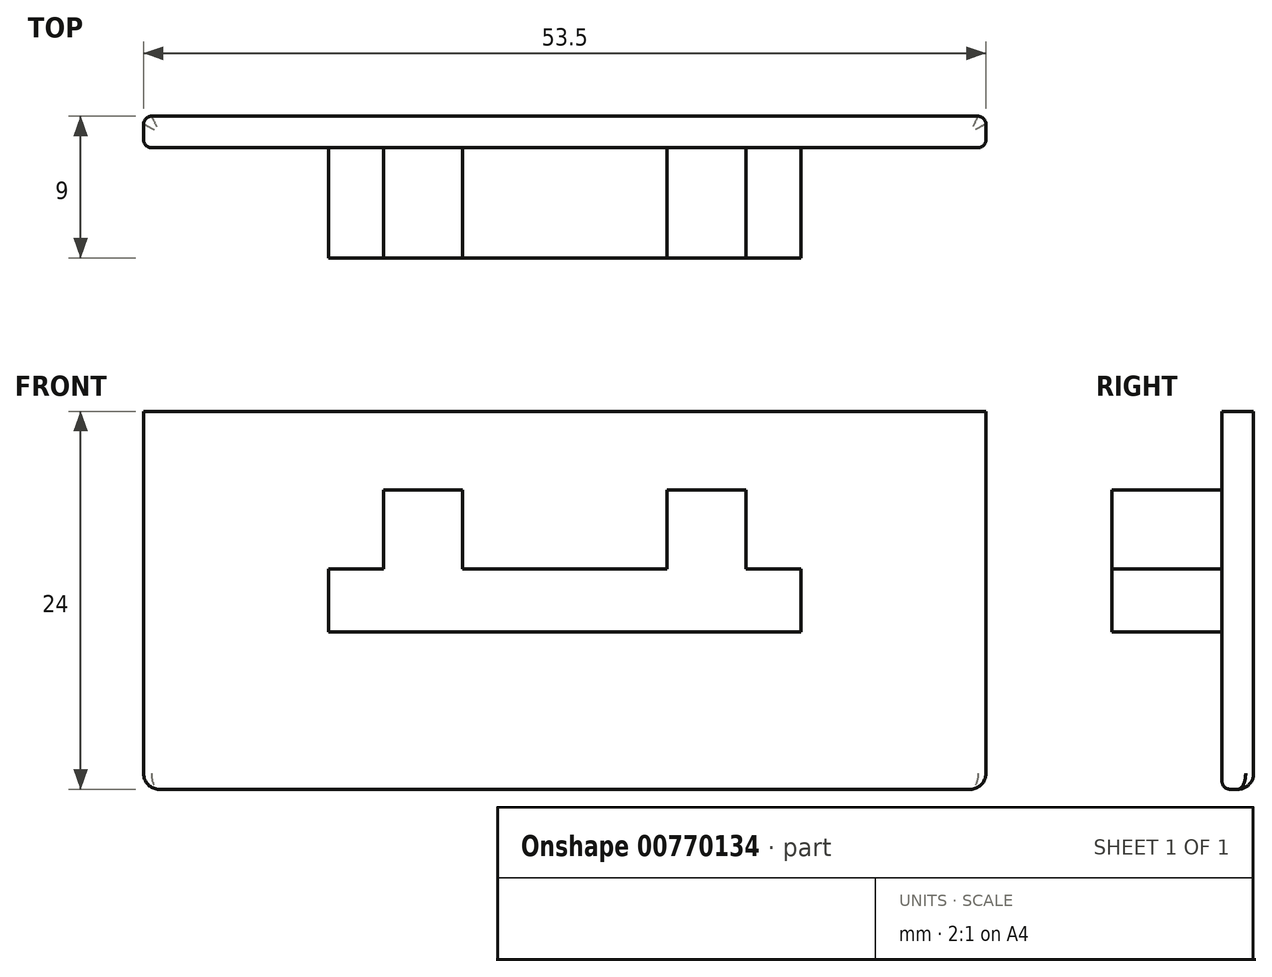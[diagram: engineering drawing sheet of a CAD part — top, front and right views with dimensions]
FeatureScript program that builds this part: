
annotation { "Feature Type Name" : "Feature", "Feature Type Description" : "" }
export const myFeature = defineFeature(function(context is Context, id is Id, definition is map)
    precondition{}
    {
        {
            var Q0;
            Q0=qCreatedBy(makeId("Front.planeOp"),FACE);
            var sketch = newSketch(context, id + "F0", { "sketchPlane" : qUnion([Q0])});
            skLineSegment(sketch, "E0.bottom", {"start": v(0, 0) * mm, "end": v(53.5, 0) * mm});
            skLineSegment(sketch, "E0.top", {"start": v(0, 24) * mm, "end": v(53.5, 24) * mm});
            skLineSegment(sketch, "E0.left", {"start": v(0, 0) * mm, "end": v(0, 24) * mm});
            skLineSegment(sketch, "E0.right", {"start": v(53.5, 0) * mm, "end": v(53.5, 24) * mm});
            skSolve(sketch);
        }
        {
            var Q0;
            Q0=qSketchRegion(id+"F0",true);
            extrude(context, id + "F1", {"entities" : qUnion([Q0]), "depth" : 2 * mm, "offsetDistance" : 25 * mm});
        }
        {
            var Q0;
            Q0=makeQuery(id+"F1.opExtrude","CAP_FACE",FACE,{"disambiguationData":[OSD([sQuery(id+"F0.wireOp",EDGE,"E0.bottom"),sQuery(id+"F0.wireOp",EDGE,"E0.top"),sQuery(id+"F0.wireOp",EDGE,"E0.left"),sQuery(id+"F0.wireOp",EDGE,"E0.right")])],"isStart":false});
            var sketch = newSketch(context, id + "F2", { "sketchPlane" : qUnion([Q0])});
            skLineSegment(sketch, "E1.bottom", {"start": v(11.75, 14) * mm, "end": v(15.25, 14) * mm});
            skLineSegment(sketch, "E1.top", {"start": v(11.75, 10) * mm, "end": v(41.75, 10) * mm});
            skLineSegment(sketch, "E1.left", {"start": v(11.75, 14) * mm, "end": v(11.75, 10) * mm});
            skLineSegment(sketch, "E1.right", {"start": v(41.75, 14) * mm, "end": v(41.75, 10) * mm});
            skLineSegment(sketch, "E2.top", {"start": v(38.25, 19) * mm, "end": v(33.25, 19) * mm});
            skLineSegment(sketch, "E2.left", {"start": v(38.25, 14) * mm, "end": v(38.25, 19) * mm});
            skLineSegment(sketch, "E2.right", {"start": v(33.25, 14) * mm, "end": v(33.25, 19) * mm});
            skLineSegment(sketch, "E3.top", {"start": v(20.25, 19) * mm, "end": v(15.25, 19) * mm});
            skLineSegment(sketch, "E3.left", {"start": v(20.25, 14) * mm, "end": v(20.25, 19) * mm});
            skLineSegment(sketch, "E3.right", {"start": v(15.25, 14) * mm, "end": v(15.25, 19) * mm});
            skLineSegment(sketch, "E4.trimOffspring", {"start": v(20.25, 14) * mm, "end": v(33.25, 14) * mm});
            skLineSegment(sketch, "E5.trimOffspring", {"start": v(38.25, 14) * mm, "end": v(41.75, 14) * mm});
            skSolve(sketch);
        }
        {
            var Q0;
            Q0=qSketchRegion(id+"F2",true);
            extrude(context, id + "F3", {"entities" : qUnion([Q0]), "operationType" : NewBodyOperationType.ADD, "depth" : 7 * mm, "offsetDistance" : 25 * mm});
        }
        {
            var Q0;
            Q0=makeQuery(id+"F1.opExtrude","SWEPT_EDGE",EDGE,{"disambiguationData":[OSD([sQuery(id+"F0.wireOp",EDGE,"E0.bottom"),sQuery(id+"F0.wireOp",EDGE,"E0.right")])]});
            var Q1;
            Q1=makeQuery(id+"F1.opExtrude","SWEPT_EDGE",EDGE,{"disambiguationData":[OSD([sQuery(id+"F0.wireOp",EDGE,"E0.bottom"),sQuery(id+"F0.wireOp",EDGE,"E0.left")])]});
            var Q2;
            Q2=makeQuery(id+"F1.opExtrude","CAP_EDGE",EDGE,{"disambiguationData":[OSD([sQuery(id+"F0.wireOp",EDGE,"E0.bottom")])],"isStart":true});
            fillet(context, id + "F4", {"entities" : qUnion([Q0, Q1, Q2]), "radius" : 1 * mm, "tangentPropagation" : true, "allowEdgeOverflow" : false});
        }
        {
            var Q0;
            Q0=makeQuery(id+"F1.opExtrude","CAP_EDGE",EDGE,{"disambiguationData":[OSD([sQuery(id+"F0.wireOp",EDGE,"E0.left")])],"isStart":false});
            var Q1;
            Q1=makeQuery(id+"F1.opExtrude","CAP_EDGE",EDGE,{"disambiguationData":[OSD([sQuery(id+"F0.wireOp",EDGE,"E0.right")])],"isStart":false});
            var Q2;
            Q2=makeQuery(id+"F1.opExtrude","CAP_EDGE",EDGE,{"disambiguationData":[OSD([sQuery(id+"F0.wireOp",EDGE,"E0.right")])],"isStart":true});
            var Q3;
            Q3=makeQuery(id+"F1.opExtrude","CAP_EDGE",EDGE,{"disambiguationData":[OSD([sQuery(id+"F0.wireOp",EDGE,"E0.left")])],"isStart":true});
            fillet(context, id + "F5", {"entities" : qUnion([Q0, Q1, Q2, Q3]), "radius" : 0.5 * mm, "tangentPropagation" : true, "allowEdgeOverflow" : false});
        }
    });
